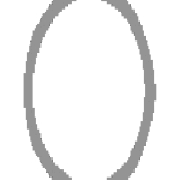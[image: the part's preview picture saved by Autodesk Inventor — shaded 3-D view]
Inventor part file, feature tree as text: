
AUTODESK INVENTOR PART (.ipt)
format: ipt  version: 2021 (Build 250183000, 183)  size: 110,080 bytes
history: native  units: in
note: dims shown in document units (in); Inventor stores cm internally (conversion verified against a paired STEP export)
features: other x4, sketch x3, plane x1
ambient origin geometry x8: Origin, YZ Plane, XZ Plane, XY Plane, X Axis, Y Axis, Z Axis, Center Point
bodies: Solid1 (feature_tree), Body (feature_tree)
feature tree (8):
  other  "Driven Length"
  other  "Frame Generator"
  other  "Start Plane"
  other  "End Plane"
  sketch  "Sketch"  dims[d2=15.2522in d4=-0.0in d5=15.2522in d6=0.12in d7=0.0in d8=90.0deg d9=15.2522in]
  sketch  "Sketch2"  dims[d0=1.0in]
  plane  "Work Plane3"
  sketch  "Sketch3"  dims[d1=0.065in]
